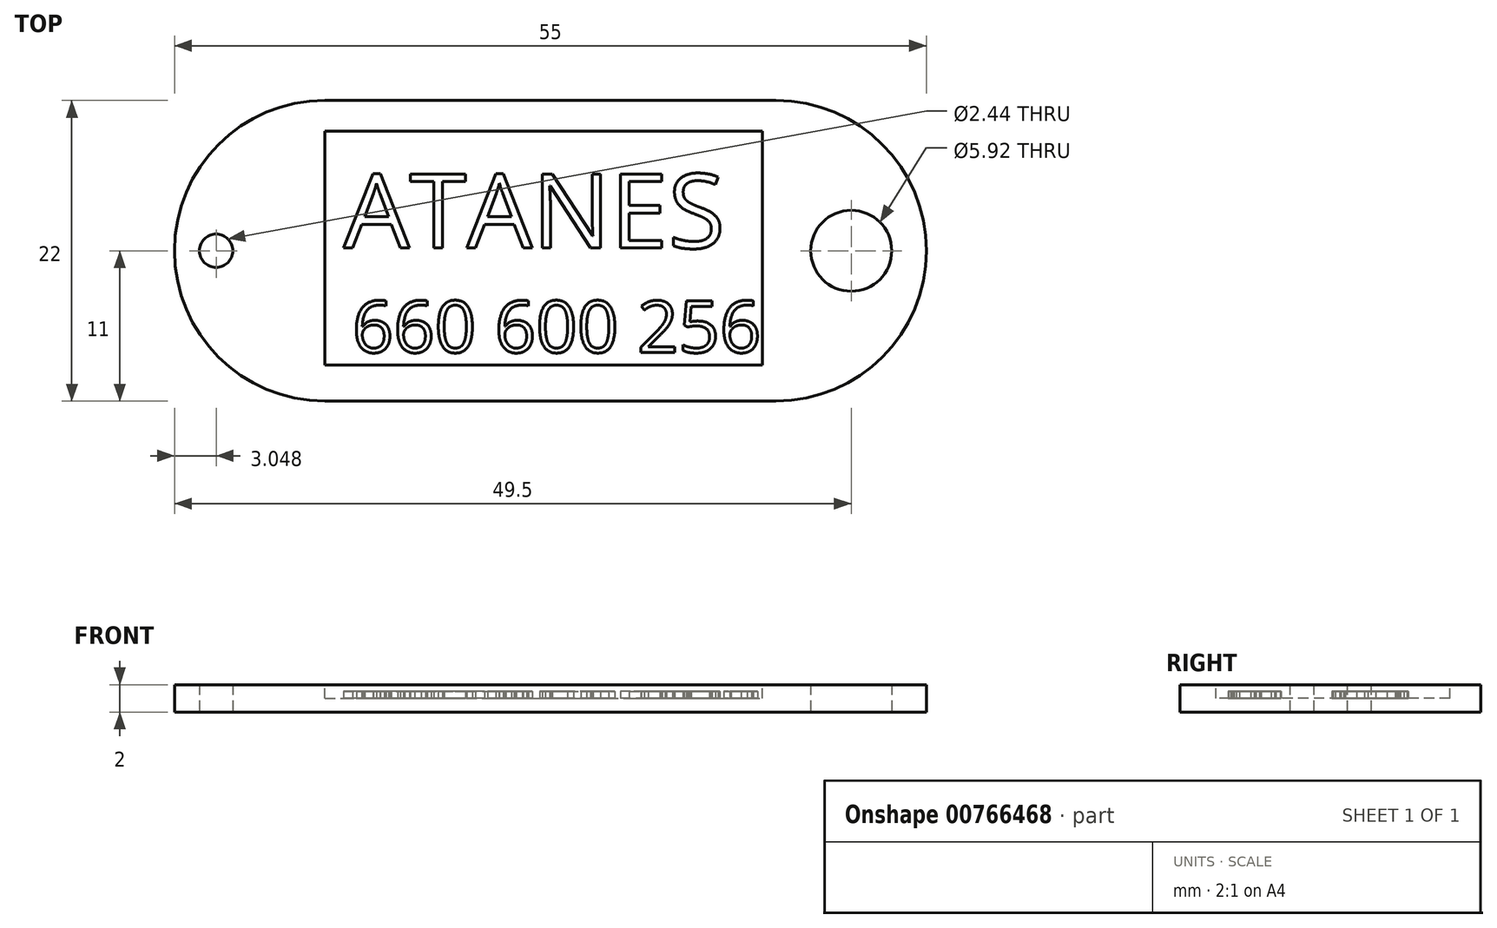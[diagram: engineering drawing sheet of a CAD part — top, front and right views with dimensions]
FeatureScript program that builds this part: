
annotation { "Feature Type Name" : "Feature", "Feature Type Description" : "" }
export const myFeature = defineFeature(function(context is Context, id is Id, definition is map)
    precondition{}
    {
        {
            var Q0;
            Q0=qCreatedBy(makeId("Top.planeOp"),FACE);
            var sketch = newSketch(context, id + "F0", { "sketchPlane" : qUnion([Q0])});
            skLineSegment(sketch, "E0.bottom", {"start": v(16.5, 11) * mm, "end": v(-16.5, 11) * mm});
            skLineSegment(sketch, "E0.top", {"start": v(16.5, -11) * mm, "end": v(-16.5, -11) * mm});
            skPoint(sketch, "E0.middle", {"position": v(0, 0) * mm});
            skArc(sketch, "E1", {"start": v(-16.5, 11) * mm, "mid": v(-27.5, 0) * mm, "end": v(-16.5, -11) * mm});
            skArc(sketch, "E2", {"start": v(16.5, -11) * mm, "mid": v(27.5, 0) * mm, "end": v(16.5, 11) * mm});
            skPoint(sketch, "E3.center.orphan", {"position": v(-22, 0) * mm});
            skPoint(sketch, "E4.center.orphan", {"position": v(22, 0) * mm});
            skPoint(sketch, "E5.orphan", {"position": v(-27.5, 11) * mm});
            skPoint(sketch, "E6.orphan", {"position": v(-27.5, -11) * mm});
            skPoint(sketch, "E7.orphan", {"position": v(27.5, -11) * mm});
            skPoint(sketch, "E8.orphan", {"position": v(27.5, 11) * mm});
            skPoint(sketch, "E9.start.orphan", {"position": v(-27.5, 0) * mm});
            skPoint(sketch, "E10.start.orphan", {"position": v(27.5, 0) * mm});
            skLineSegment(sketch, "E11", {"start": v(-16.5, -7.96) * mm, "end": v(-16.5, 7.97) * mm});
            skLineSegment(sketch, "E12", {"start": v(16.5, -7.96) * mm, "end": v(16.5, 7.97) * mm});
            skLineSegment(sketch, "E13.left", {"start": v(16.5, 7.97) * mm, "end": v(16.5, 7.97) * mm});
            skLineSegment(sketch, "E13.right", {"start": v(-16.5, 7.97) * mm, "end": v(-16.5, 7.97) * mm});
            skPoint(sketch, "E13.middle", {"position": v(0, 7.97) * mm});
            skLineSegment(sketch, "E14", {"start": v(0, -7.96) * mm, "end": v(16.5, -7.96) * mm});
            skLineSegment(sketch, "E15", {"start": v(16.5, -7.96) * mm, "end": v(-16.5, -7.96) * mm});
            skLineSegment(sketch, "E16", {"start": v(0, 7.97) * mm, "end": v(16.5, 7.97) * mm});
            skLineSegment(sketch, "E17", {"start": v(0, 7.97) * mm, "end": v(-16.5, 7.97) * mm});
            skPoint(sketch, "E18.start.orphan", {"position": v(0, 11) * mm});
            skCircle(sketch, "E19", {"center": v(-24.45, 0) * mm, "radius": 1.22 * mm});
            skCircle(sketch, "E20", {"center": v(22, 0) * mm, "radius": 2.96 * mm});
            skPoint(sketch, "E21.trimOffspring.start.orphan", {"position": v(-16.5, 9.87) * mm});
            skPoint(sketch, "E22.start.orphan", {"position": v(0, -11) * mm});
            skSolve(sketch);
        }
        {
            var Q0;
            {var subQ1=sQuery(id+"F0.wireOp",EDGE,"E11");Q0=makeQuery(id+"F0.imprint","IMPRINT",FACE,{"disambiguationData":[TD([[makeQuery(id+"F0.imprint","IMPRINT",EDGE,{"derivedFrom":subQ1}),-1.0]])]});}
            var Q1;
            Q1=makeQuery(id+"F0.imprint","IMPRINT",FACE,{"disambiguationData":[TD([[makeQuery(id+"F0.imprint","IMPRINT",EDGE,{"derivedFrom":sQuery(id+"F0.wireOp",EDGE,"E0.bottom")}),1.0]])]});
            extrude(context, id + "F1", {"entities" : qUnion([Q0, Q1]), "depth" : 2 * mm, "offsetDistance" : 25 * mm});
        }
        {
            var Q0;
            Q0=makeQuery(id+"F1.opExtrude","CAP_FACE",FACE,{"disambiguationData":[OSD([sQuery(id+"F0.wireOp",EDGE,"E0.bottom"),sQuery(id+"F0.wireOp",EDGE,"E0.top"),sQuery(id+"F0.wireOp",EDGE,"E1"),sQuery(id+"F0.wireOp",EDGE,"E2"),sQuery(id+"F0.wireOp",EDGE,"E19"),sQuery(id+"F0.wireOp",EDGE,"E20")])],"isStart":false});
            var sketch = newSketch(context, id + "F2", { "sketchPlane" : qUnion([Q0])});
            skLineSegment(sketch, "E23", {"start": v(-16.5, 8.75) * mm, "end": v(-16.5, -8.36) * mm});
            skLineSegment(sketch, "E24.bottom", {"start": v(-16.5, 8.75) * mm, "end": v(15.5, 8.75) * mm});
            skLineSegment(sketch, "E24.top", {"start": v(-16.5, -8.36) * mm, "end": v(15.5, -8.36) * mm});
            skLineSegment(sketch, "E24.right", {"start": v(15.5, 8.75) * mm, "end": v(15.5, -8.36) * mm});
            skSolve(sketch);
        }
        {
            var Q0;
            Q0=makeQuery(id+"F2.imprint","IMPRINT",FACE,{"disambiguationData":[TD([[makeQuery(id+"F2.imprint","IMPRINT",EDGE,{"derivedFrom":sQuery(id+"F2.wireOp",EDGE,"E24.bottom")}),-1.0]])]});
            extrude(context, id + "F3", {"entities" : qUnion([Q0]), "operationType" : NewBodyOperationType.REMOVE, "oppositeDirection" : true, "depth" : 1 * mm, "offsetDistance" : 25 * mm});
        }
        {
            var Q0;
            Q0=makeQuery(id+"F3.boolean.opBoolean","COPY",FACE,{"derivedFrom":makeQuery(id+"F3.opExtrude","CAP_FACE",FACE,{"disambiguationData":[OSD([sQuery(id+"F2.wireOp",EDGE,"E24.bottom"),sQuery(id+"F2.wireOp",EDGE,"E24.top"),sQuery(id+"F2.wireOp",EDGE,"E23"),sQuery(id+"F2.wireOp",EDGE,"E24.right")])],"isStart":false})});
            var sketch = newSketch(context, id + "F4", { "sketchPlane" : qUnion([Q0])});
            skText(sketch, "E25", { "text": "ATANES", "fontName": "OpenSans-Regular.ttf"});
            skPoint(sketch, "E25.secondSnap0", {"position": v(15.5, 0.2) * mm});
            skText(sketch, "E26", { "text": "660 600 256", "fontName": "OpenSans-Regular.ttf"});
            const initialGuessF4  = {"E25": [-0.01512, 0.0002, 1, 0, 0.00546], "E26": [-0.0145, -0.00744, 1, 0, 0.0038]};
            skSetInitialGuess(sketch, initialGuessF4);
            skSolve(sketch);
        }
        {
            var Q0;
            Q0 = qSketchRegion(id + "F4", true);
            extrude(context, id + "F5", {"entities" : qUnion([Q0]), "operationType" : NewBodyOperationType.ADD, "depth" : 0.5 * mm, "offsetDistance" : 25 * mm});
        }
    });
